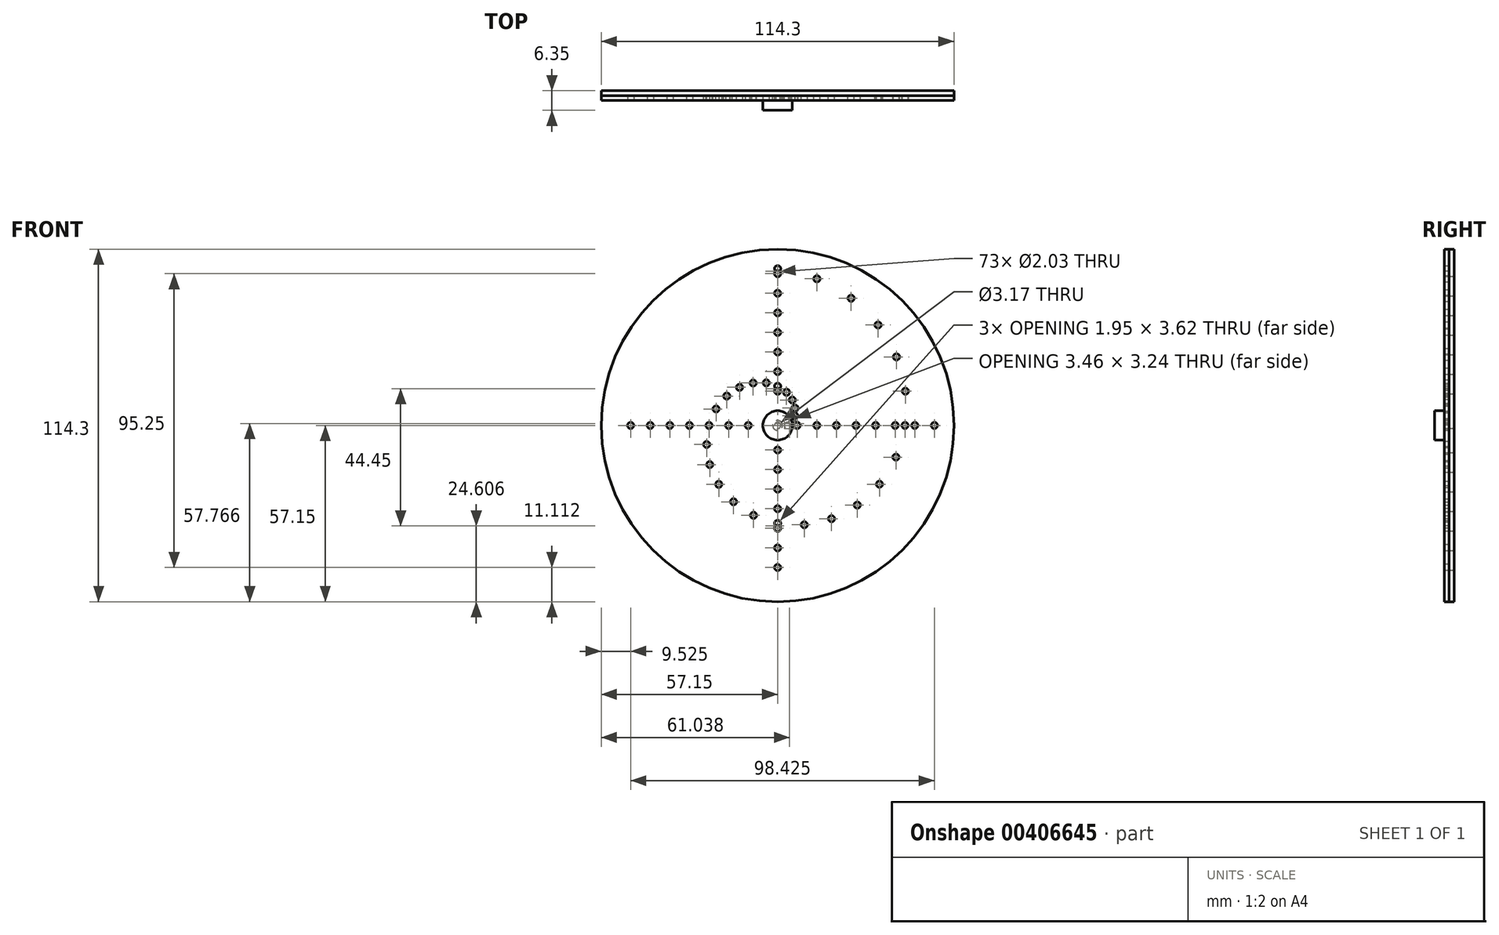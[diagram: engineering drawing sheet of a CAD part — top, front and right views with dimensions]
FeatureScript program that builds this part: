
annotation { "Feature Type Name" : "Feature", "Feature Type Description" : "" }
export const myFeature = defineFeature(function(context is Context, id is Id, definition is map)
    precondition{}
    {
        {
            var Q0;
            Q0=qCreatedBy(makeId("Front.planeOp"),FACE);
            var sketch = newSketch(context, id + "F0", { "sketchPlane" : qUnion([Q0])});
            skCircle(sketch, "E0", {"center": v(0, 0) * mm, "radius": 50.8 * mm, "construction": true});
            skCircle(sketch, "E1", {"center": v(0, 0) * mm, "radius": 1.59 * mm});
            skCircle(sketch, "E2.0", {"center": v(0, 0) * mm, "radius": 3.17 * mm, "construction": true});
            skCircle(sketch, "E3.0", {"center": v(0, 0) * mm, "radius": 4.76 * mm, "construction": true});
            skCircle(sketch, "E4.0", {"center": v(0, 0) * mm, "radius": 6.35 * mm, "construction": true});
            skLineSegment(sketch, "E5", {"start": v(0, 0) * mm, "end": v(67.63, 0) * mm, "construction": true});
            skCircle(sketch, "E6", {"center": v(3.17, 0) * mm, "radius": 1.02 * mm});
            skLineSegment(sketch, "E7", {"start": v(0, 0) * mm, "end": v(1.59, 0) * mm});
            skLineSegment(sketch, "E8", {"start": v(0, 0) * mm, "end": v(49.07, 13.15) * mm, "construction": true});
            skLineSegment(sketch, "E9.1.0", {"start": v(0, 0) * mm, "end": v(44, 25.4) * mm, "construction": true});
            skLineSegment(sketch, "E9.2.0", {"start": v(0, 0) * mm, "end": v(35.92, 35.92) * mm, "construction": true});
            skLineSegment(sketch, "E9.3.0", {"start": v(0, 0) * mm, "end": v(25.4, 44) * mm, "construction": true});
            skLineSegment(sketch, "E9.4.0", {"start": v(0, 0) * mm, "end": v(13.15, 49.07) * mm, "construction": true});
            skLineSegment(sketch, "E9.5.0", {"start": v(0, 0) * mm, "end": v(0, 50.8) * mm, "construction": true});
            skLineSegment(sketch, "E9.6.0", {"start": v(0, 0) * mm, "end": v(-13.15, 49.07) * mm, "construction": true});
            skLineSegment(sketch, "E9.7.0", {"start": v(0, 0) * mm, "end": v(-25.4, 44) * mm, "construction": true});
            skLineSegment(sketch, "E9.8.0", {"start": v(0, 0) * mm, "end": v(-35.92, 35.92) * mm, "construction": true});
            skLineSegment(sketch, "E9.9.0", {"start": v(0, 0) * mm, "end": v(-44, 25.4) * mm, "construction": true});
            skLineSegment(sketch, "E9.10.0", {"start": v(0, 0) * mm, "end": v(-49.07, 13.15) * mm, "construction": true});
            skLineSegment(sketch, "E9.11.0", {"start": v(0, 0) * mm, "end": v(-50.8, 0) * mm, "construction": true});
            skLineSegment(sketch, "E9.anchor2", {"start": v(0, 0) * mm, "end": v(-50.8, 0) * mm, "construction": true});
            skCircle(sketch, "E10.0", {"center": v(0, 0) * mm, "radius": 7.94 * mm, "construction": true});
            skCircle(sketch, "E11.0", {"center": v(0, 0) * mm, "radius": 9.53 * mm, "construction": true});
            skCircle(sketch, "E12.0", {"center": v(0, 0) * mm, "radius": 11.11 * mm, "construction": true});
            skCircle(sketch, "E13.0", {"center": v(0, 0) * mm, "radius": 12.7 * mm, "construction": true});
            skCircle(sketch, "E14.0", {"center": v(0, 0) * mm, "radius": 14.29 * mm, "construction": true});
            skCircle(sketch, "E15.0", {"center": v(0, 0) * mm, "radius": 15.88 * mm, "construction": true});
            skCircle(sketch, "E16.0", {"center": v(0, 0) * mm, "radius": 17.46 * mm, "construction": true});
            skCircle(sketch, "E17.0", {"center": v(0, 0) * mm, "radius": 19.05 * mm, "construction": true});
            skCircle(sketch, "E18.0", {"center": v(0, 0) * mm, "radius": 20.64 * mm, "construction": true});
            skCircle(sketch, "E19.0", {"center": v(0, 0) * mm, "radius": 22.22 * mm, "construction": true});
            skCircle(sketch, "E20.0", {"center": v(0, 0) * mm, "radius": 23.81 * mm, "construction": true});
            skCircle(sketch, "E21.0", {"center": v(0, 0) * mm, "radius": 25.4 * mm, "construction": true});
            skCircle(sketch, "E22.0", {"center": v(0, 0) * mm, "radius": 26.99 * mm, "construction": true});
            skCircle(sketch, "E23.0", {"center": v(0, 0) * mm, "radius": 28.57 * mm, "construction": true});
            skCircle(sketch, "E24.0", {"center": v(0, 0) * mm, "radius": 30.16 * mm, "construction": true});
            skCircle(sketch, "E25.0", {"center": v(0, 0) * mm, "radius": 31.75 * mm, "construction": true});
            skCircle(sketch, "E26", {"center": v(4.6, 1.23) * mm, "radius": 1.02 * mm});
            skCircle(sketch, "E27", {"center": v(5.5, 3.17) * mm, "radius": 1.02 * mm});
            skCircle(sketch, "E28", {"center": v(5.61, 5.61) * mm, "radius": 1.02 * mm});
            skCircle(sketch, "E29", {"center": v(4.76, 8.25) * mm, "radius": 1.02 * mm});
            skCircle(sketch, "E30", {"center": v(2.88, 10.73) * mm, "radius": 1.02 * mm});
            skCircle(sketch, "E31", {"center": v(0, 12.7) * mm, "radius": 1.02 * mm});
            skCircle(sketch, "E32", {"center": v(-3.7, 13.8) * mm, "radius": 1.02 * mm});
            skCircle(sketch, "E33", {"center": v(-7.94, 13.75) * mm, "radius": 1.02 * mm});
            skCircle(sketch, "E34", {"center": v(-12.35, 12.35) * mm, "radius": 1.02 * mm});
            skCircle(sketch, "E35", {"center": v(-16.5, 9.53) * mm, "radius": 1.02 * mm});
            skCircle(sketch, "E36", {"center": v(-19.93, 5.34) * mm, "radius": 1.02 * mm});
            skCircle(sketch, "E37", {"center": v(-22.22, 0) * mm, "radius": 1.02 * mm});
            skCircle(sketch, "E38.0", {"center": v(0, 0) * mm, "radius": 33.34 * mm, "construction": true});
            skCircle(sketch, "E39.0", {"center": v(0, 0) * mm, "radius": 34.92 * mm, "construction": true});
            skCircle(sketch, "E40.0", {"center": v(0, 0) * mm, "radius": 36.51 * mm, "construction": true});
            skCircle(sketch, "E41.0", {"center": v(0, 0) * mm, "radius": 38.1 * mm, "construction": true});
            skCircle(sketch, "E42.0", {"center": v(0, 0) * mm, "radius": 39.69 * mm, "construction": true});
            skCircle(sketch, "E43.0", {"center": v(0, 0) * mm, "radius": 41.27 * mm, "construction": true});
            skCircle(sketch, "E44.0", {"center": v(0, 0) * mm, "radius": 42.86 * mm, "construction": true});
            skCircle(sketch, "E45.0", {"center": v(0, 0) * mm, "radius": 44.45 * mm, "construction": true});
            skCircle(sketch, "E46.0", {"center": v(0, 0) * mm, "radius": 46.04 * mm, "construction": true});
            skCircle(sketch, "E47.0", {"center": v(0, 0) * mm, "radius": 47.62 * mm, "construction": true});
            skCircle(sketch, "E48.0", {"center": v(0, 0) * mm, "radius": 49.21 * mm, "construction": true});
            skLineSegment(sketch, "E49.MirrorCS", {"start": v(0, 0) * mm, "end": v(-49.07, -13.15) * mm, "construction": true});
            skLineSegment(sketch, "E50.MirrorCS", {"start": v(0, 0) * mm, "end": v(-44, -25.4) * mm, "construction": true});
            skLineSegment(sketch, "E51.MirrorCS", {"start": v(0, 0) * mm, "end": v(-35.92, -35.92) * mm, "construction": true});
            skLineSegment(sketch, "E52.MirrorCS", {"start": v(0, 0) * mm, "end": v(-25.4, -44) * mm, "construction": true});
            skLineSegment(sketch, "E53.MirrorCS", {"start": v(0, 0) * mm, "end": v(-13.15, -49.07) * mm, "construction": true});
            skLineSegment(sketch, "E54.MirrorCS", {"start": v(0, 0) * mm, "end": v(0, -50.8) * mm, "construction": true});
            skLineSegment(sketch, "E55.MirrorCS", {"start": v(0, 0) * mm, "end": v(13.15, -49.07) * mm, "construction": true});
            skLineSegment(sketch, "E56.MirrorCS", {"start": v(0, 0) * mm, "end": v(25.4, -44) * mm, "construction": true});
            skLineSegment(sketch, "E57.MirrorCS", {"start": v(0, 0) * mm, "end": v(35.92, -35.92) * mm, "construction": true});
            skLineSegment(sketch, "E58.MirrorCS", {"start": v(0, 0) * mm, "end": v(44, -25.4) * mm, "construction": true});
            skLineSegment(sketch, "E59.MirrorCS", {"start": v(0, 0) * mm, "end": v(49.07, -13.15) * mm, "construction": true});
            skCircle(sketch, "E60", {"center": v(-23, -6.16) * mm, "radius": 1.02 * mm});
            skCircle(sketch, "E61", {"center": v(-22, -12.7) * mm, "radius": 1.02 * mm});
            skCircle(sketch, "E62", {"center": v(-19.08, -19.08) * mm, "radius": 1.02 * mm});
            skCircle(sketch, "E63", {"center": v(-14.29, -24.75) * mm, "radius": 1.02 * mm});
            skCircle(sketch, "E64", {"center": v(-7.8, -29.13) * mm, "radius": 1.02 * mm});
            skCircle(sketch, "E65", {"center": v(0, -31.75) * mm, "radius": 1.02 * mm});
            skCircle(sketch, "E66", {"center": v(8.63, -32.2) * mm, "radius": 1.02 * mm});
            skCircle(sketch, "E67", {"center": v(17.46, -30.25) * mm, "radius": 1.02 * mm});
            skCircle(sketch, "E68", {"center": v(25.82, -25.82) * mm, "radius": 1.02 * mm});
            skCircle(sketch, "E69", {"center": v(33, -19.05) * mm, "radius": 1.02 * mm});
            skCircle(sketch, "E70", {"center": v(38.34, -10.27) * mm, "radius": 1.02 * mm});
            skCircle(sketch, "E71", {"center": v(41.27, 0) * mm, "radius": 1.02 * mm});
            skCircle(sketch, "E72", {"center": v(41.4, 11.1) * mm, "radius": 1.02 * mm});
            skCircle(sketch, "E73", {"center": v(38.5, 22.22) * mm, "radius": 1.02 * mm});
            skCircle(sketch, "E74", {"center": v(32.55, 32.55) * mm, "radius": 1.02 * mm});
            skCircle(sketch, "E75", {"center": v(23.81, 41.24) * mm, "radius": 1.02 * mm});
            skCircle(sketch, "E76", {"center": v(12.74, 47.54) * mm, "radius": 1.02 * mm});
            skCircle(sketch, "E77.0", {"center": v(0, 0) * mm, "radius": 57.15 * mm});
            skCircle(sketch, "E78", {"center": v(0, 50.8) * mm, "radius": 1.02 * mm});
            skSolve(sketch);
        }
        {
            var Q0;
            Q0 = qSketchRegion(id + "F0", true);
            extrude(context, id + "F1", {"entities" : qUnion([Q0]), "depth" : 1.59 * mm});
        }
        {
            var Q0;
            Q0=makeQuery(id+"F1.opExtrude","CAP_FACE",FACE,{"disambiguationData":[OSD([sQuery(id+"F0.wireOp",EDGE,"E1"),sQuery(id+"F0.wireOp",EDGE,"E6"),sQuery(id+"F0.wireOp",EDGE,"E26"),sQuery(id+"F0.wireOp",EDGE,"E27"),sQuery(id+"F0.wireOp",EDGE,"E28"),sQuery(id+"F0.wireOp",EDGE,"E29"),sQuery(id+"F0.wireOp",EDGE,"E30"),sQuery(id+"F0.wireOp",EDGE,"E31"),sQuery(id+"F0.wireOp",EDGE,"E32"),sQuery(id+"F0.wireOp",EDGE,"E33"),sQuery(id+"F0.wireOp",EDGE,"E34"),sQuery(id+"F0.wireOp",EDGE,"E35"),sQuery(id+"F0.wireOp",EDGE,"E36"),sQuery(id+"F0.wireOp",EDGE,"E37"),sQuery(id+"F0.wireOp",EDGE,"E60"),sQuery(id+"F0.wireOp",EDGE,"E61"),sQuery(id+"F0.wireOp",EDGE,"E62"),sQuery(id+"F0.wireOp",EDGE,"E63"),sQuery(id+"F0.wireOp",EDGE,"E64"),sQuery(id+"F0.wireOp",EDGE,"E65"),sQuery(id+"F0.wireOp",EDGE,"E66"),sQuery(id+"F0.wireOp",EDGE,"E67"),sQuery(id+"F0.wireOp",EDGE,"E68"),sQuery(id+"F0.wireOp",EDGE,"E69"),sQuery(id+"F0.wireOp",EDGE,"E70"),sQuery(id+"F0.wireOp",EDGE,"E71"),sQuery(id+"F0.wireOp",EDGE,"E72"),sQuery(id+"F0.wireOp",EDGE,"E73"),sQuery(id+"F0.wireOp",EDGE,"E74"),sQuery(id+"F0.wireOp",EDGE,"E75"),sQuery(id+"F0.wireOp",EDGE,"E76"),sQuery(id+"F0.wireOp",EDGE,"E77.0"),sQuery(id+"F0.wireOp",EDGE,"E78")])],"isStart":false});
            var sketch = newSketch(context, id + "F2", { "sketchPlane" : qUnion([Q0])});
            skCircle(sketch, "E79.0", {"center": v(0, 0) * mm, "radius": 57.15 * mm, "construction": true});
            skCircle(sketch, "E80", {"center": v(0, 0) * mm, "radius": 12.7 * mm});
            skCircle(sketch, "E81", {"center": v(0, 0) * mm, "radius": 25.4 * mm});
            skCircle(sketch, "E82", {"center": v(0, 0) * mm, "radius": 38.1 * mm});
            skCircle(sketch, "E83", {"center": v(0, 0) * mm, "radius": 6.35 * mm});
            skCircle(sketch, "E84", {"center": v(0, 0) * mm, "radius": 19.05 * mm});
            skCircle(sketch, "E85", {"center": v(0, 0) * mm, "radius": 31.75 * mm});
            skCircle(sketch, "E86", {"center": v(0, 0) * mm, "radius": 44.45 * mm});
            skCircle(sketch, "E87", {"center": v(0, 0) * mm, "radius": 50.8 * mm});
            skSolve(sketch);
        }
        {
            var Q0;
            Q0=makeQuery(id+"F2.imprint","IMPRINT",FACE,{"disambiguationData":[TD([[makeQuery(id+"F2.imprint","IMPRINT",EDGE,{"derivedFrom":makeQuery(id+"F1.opExtrude","CAP_EDGE",EDGE,{"disambiguationData":[OSD([sQuery(id+"F0.wireOp",EDGE,"E74")])],"isStart":false})}),-1.0]])]});
            var sketch = newSketch(context, id + "F3", { "sketchPlane" : qUnion([Q0])});
            skCircle(sketch, "E88", {"center": v(0, 0) * mm, "radius": 4.76 * mm});
            skSolve(sketch);
        }
        {
            var Q0;
            Q0 = qSketchRegion(id + "F3", true);
            extrude(context, id + "F4", {"entities" : qUnion([Q0]), "depth" : 3.17 * mm});
        }
        {
            var Q0;
            Q0=makeQuery(id+"F2.imprint","IMPRINT",FACE,{"disambiguationData":[TD([[makeQuery(id+"F2.imprint","IMPRINT",EDGE,{"derivedFrom":makeQuery(id+"F1.opExtrude","CAP_EDGE",EDGE,{"disambiguationData":[OSD([sQuery(id+"F0.wireOp",EDGE,"E77.0")])],"isStart":false})}),1.0]])]});
            var sketch = newSketch(context, id + "F5", { "sketchPlane" : qUnion([Q0])});
            skCircle(sketch, "E89.0", {"center": v(0, 0) * mm, "radius": 57.15 * mm});
            skCircle(sketch, "E89.1", {"center": v(0, 0) * mm, "radius": 50.8 * mm, "construction": true});
            skCircle(sketch, "E89.2", {"center": v(0, 0) * mm, "radius": 44.45 * mm, "construction": true});
            skCircle(sketch, "E89.3", {"center": v(0, 0) * mm, "radius": 38.1 * mm, "construction": true});
            skCircle(sketch, "E89.4", {"center": v(0, 0) * mm, "radius": 31.75 * mm, "construction": true});
            skCircle(sketch, "E89.5", {"center": v(0, 0) * mm, "radius": 25.4 * mm, "construction": true});
            skCircle(sketch, "E89.6", {"center": v(0, 0) * mm, "radius": 19.05 * mm, "construction": true});
            skCircle(sketch, "E89.7", {"center": v(0, 0) * mm, "radius": 12.7 * mm, "construction": true});
            skCircle(sketch, "E89.8", {"center": v(0, 0) * mm, "radius": 6.35 * mm, "construction": true});
            skLineSegment(sketch, "E90", {"start": v(0, 0) * mm, "end": v(57.15, 0) * mm, "construction": true});
            skCircle(sketch, "E91", {"center": v(6.35, 0) * mm, "radius": 1.02 * mm});
            skCircle(sketch, "E92", {"center": v(12.7, 0) * mm, "radius": 1.02 * mm});
            skCircle(sketch, "E93", {"center": v(19.05, 0) * mm, "radius": 1.02 * mm});
            skCircle(sketch, "E94", {"center": v(25.4, 0) * mm, "radius": 1.02 * mm});
            skCircle(sketch, "E95", {"center": v(31.75, 0) * mm, "radius": 1.02 * mm});
            skCircle(sketch, "E96", {"center": v(38.1, 0) * mm, "radius": 1.02 * mm});
            skCircle(sketch, "E97", {"center": v(44.45, 0) * mm, "radius": 1.02 * mm});
            skCircle(sketch, "E98", {"center": v(50.8, 0) * mm, "radius": 1.02 * mm});
            skCircle(sketch, "E99.0", {"center": v(5.61, 5.61) * mm, "radius": 1.02 * mm, "construction": true});
            skLineSegment(sketch, "E100.anchor1", {"start": v(0, 0) * mm, "end": v(6.35, 0) * mm, "construction": true});
            skCircle(sketch, "E101", {"center": v(0, 0) * mm, "radius": 57.15 * mm, "construction": true});
            skCircle(sketch, "E102.1.0", {"center": v(0, -25.4) * mm, "radius": 1.02 * mm, "construction": true});
            skCircle(sketch, "E102.1.1", {"center": v(0, -19.05) * mm, "radius": 1.02 * mm, "construction": true});
            skCircle(sketch, "E102.1.2", {"center": v(0, -12.7) * mm, "radius": 1.02 * mm, "construction": true});
            skCircle(sketch, "E102.1.3", {"center": v(0, -38.1) * mm, "radius": 1.02 * mm, "construction": true});
            skCircle(sketch, "E102.1.4", {"center": v(0, -31.75) * mm, "radius": 1.02 * mm, "construction": true});
            skCircle(sketch, "E102.1.5", {"center": v(0, -44.45) * mm, "radius": 1.02 * mm, "construction": true});
            skCircle(sketch, "E102.1.6", {"center": v(0, -50.8) * mm, "radius": 1.02 * mm, "construction": true});
            skCircle(sketch, "E102.1.7", {"center": v(0, -6.35) * mm, "radius": 1.02 * mm, "construction": true});
            skCircle(sketch, "E102.2.0", {"center": v(-25.4, 0) * mm, "radius": 1.02 * mm, "construction": true});
            skCircle(sketch, "E102.2.1", {"center": v(-19.05, 0) * mm, "radius": 1.02 * mm, "construction": true});
            skCircle(sketch, "E102.2.2", {"center": v(-12.7, 0) * mm, "radius": 1.02 * mm, "construction": true});
            skCircle(sketch, "E102.2.3", {"center": v(-38.1, 0) * mm, "radius": 1.02 * mm, "construction": true});
            skCircle(sketch, "E102.2.4", {"center": v(-31.75, 0) * mm, "radius": 1.02 * mm, "construction": true});
            skCircle(sketch, "E102.2.5", {"center": v(-44.45, 0) * mm, "radius": 1.02 * mm, "construction": true});
            skCircle(sketch, "E102.2.6", {"center": v(-50.8, 0) * mm, "radius": 1.02 * mm, "construction": true});
            skCircle(sketch, "E102.2.7", {"center": v(-6.35, 0) * mm, "radius": 1.02 * mm, "construction": true});
            skCircle(sketch, "E102.3.0", {"center": v(0, 25.4) * mm, "radius": 1.02 * mm, "construction": true});
            skCircle(sketch, "E102.3.1", {"center": v(0, 19.05) * mm, "radius": 1.02 * mm, "construction": true});
            skCircle(sketch, "E102.3.2", {"center": v(0, 12.7) * mm, "radius": 1.02 * mm, "construction": true});
            skCircle(sketch, "E102.3.3", {"center": v(0, 38.1) * mm, "radius": 1.02 * mm, "construction": true});
            skCircle(sketch, "E102.3.4", {"center": v(0, 31.75) * mm, "radius": 1.02 * mm, "construction": true});
            skCircle(sketch, "E102.3.5", {"center": v(0, 44.45) * mm, "radius": 1.02 * mm, "construction": true});
            skCircle(sketch, "E102.3.6", {"center": v(0, 50.8) * mm, "radius": 1.02 * mm, "construction": true});
            skCircle(sketch, "E102.3.7", {"center": v(0, 6.35) * mm, "radius": 1.02 * mm, "construction": true});
            skLineSegment(sketch, "E102.anchor2", {"start": v(0, 0) * mm, "end": v(0, 6.35) * mm, "construction": true});
            skSolve(sketch);
        }
        {
            var Q0;
            Q0 = qSketchRegion(id + "F5", true);
            extrude(context, id + "F6", {"entities" : qUnion([Q0]), "oppositeDirection" : true, "depth" : 3.17 * mm});
        }
        {
            var Q0;
            Q0=makeQuery(id+"F2.imprint","IMPRINT",FACE,{"disambiguationData":[TD([[makeQuery(id+"F2.imprint","IMPRINT",EDGE,{"derivedFrom":makeQuery(id+"F1.opExtrude","CAP_EDGE",EDGE,{"disambiguationData":[OSD([sQuery(id+"F0.wireOp",EDGE,"E77.0")])],"isStart":false})}),1.0]])]});
            var sketch = newSketch(context, id + "F7", { "sketchPlane" : qUnion([Q0])});
            skCircle(sketch, "E103.0", {"center": v(0, -6.35) * mm, "radius": 1.02 * mm, "construction": true});
            skLineSegment(sketch, "E104", {"start": v(0, 0) * mm, "end": v(0, -57.15) * mm, "construction": true});
            skCircle(sketch, "E105.0", {"center": v(0, 0) * mm, "radius": 57.15 * mm, "construction": true});
            skCircle(sketch, "E106.2", {"center": v(0, -12.7) * mm, "radius": 1.02 * mm, "construction": true});
            skCircle(sketch, "E106.3", {"center": v(0, -19.05) * mm, "radius": 1.02 * mm, "construction": true});
            skCircle(sketch, "E106.4", {"center": v(0, -25.4) * mm, "radius": 1.02 * mm, "construction": true});
            skCircle(sketch, "E106.5", {"center": v(0, -31.75) * mm, "radius": 1.02 * mm, "construction": true});
            skCircle(sketch, "E106.6", {"center": v(0, -38.1) * mm, "radius": 1.02 * mm, "construction": true});
            skCircle(sketch, "E106.7", {"center": v(0, -44.45) * mm, "radius": 1.02 * mm, "construction": true});
            skCircle(sketch, "E106.8", {"center": v(0, -50.8) * mm, "radius": 1.02 * mm, "construction": true});
            skCircle(sketch, "E107.0.1.0", {"center": v(0, -33.34) * mm, "radius": 1.02 * mm});
            skCircle(sketch, "E107.0.1.1", {"center": v(0, -52.39) * mm, "radius": 1.02 * mm, "construction": true});
            skCircle(sketch, "E107.0.1.2", {"center": v(0, -26.99) * mm, "radius": 1.02 * mm});
            skCircle(sketch, "E107.0.1.3", {"center": v(0, -14.29) * mm, "radius": 1.02 * mm});
            skCircle(sketch, "E107.0.1.4", {"center": v(0, -20.64) * mm, "radius": 1.02 * mm});
            skCircle(sketch, "E107.0.1.5", {"center": v(0, -39.69) * mm, "radius": 1.02 * mm});
            skCircle(sketch, "E107.0.1.6", {"center": v(0, -46.04) * mm, "radius": 1.02 * mm});
            skCircle(sketch, "E107.0.1.7", {"center": v(0, -7.94) * mm, "radius": 1.02 * mm});
            skLineSegment(sketch, "E107.direction1", {"start": v(0, -50.8) * mm, "end": v(25.4, -50.8) * mm, "construction": true});
            skLineSegment(sketch, "E107.direction2", {"start": v(0, -50.8) * mm, "end": v(0, -52.39) * mm, "construction": true});
            skSolve(sketch);
        }
        {
            var Q0;
            Q0 = qSketchRegion(id + "F7", true);
            extrude(context, id + "F8", {"entities" : qUnion([Q0]), "operationType" : NewBodyOperationType.REMOVE, "endBound" : BoundingType.THROUGH_ALL, "oppositeDirection" : true, "depth" : 25.4 * mm});
        }
        {
            var Q0;
            Q0=makeQuery(id+"F2.imprint","IMPRINT",FACE,{"disambiguationData":[TD([[makeQuery(id+"F2.imprint","IMPRINT",EDGE,{"derivedFrom":makeQuery(id+"F1.opExtrude","CAP_EDGE",EDGE,{"disambiguationData":[OSD([sQuery(id+"F0.wireOp",EDGE,"E28")])],"isStart":false})}),-1.0]])]});
            var sketch = newSketch(context, id + "F9", { "sketchPlane" : qUnion([Q0])});
            skCircle(sketch, "E108.0", {"center": v(-6.35, 0) * mm, "radius": 1.02 * mm, "construction": true});
            skCircle(sketch, "E109", {"center": v(-9.53, 0) * mm, "radius": 1.02 * mm});
            skCircle(sketch, "E110.0", {"center": v(0, 6.35) * mm, "radius": 1.02 * mm, "construction": true});
            skCircle(sketch, "E111", {"center": v(0, 11.11) * mm, "radius": 1.02 * mm});
            skCircle(sketch, "E112.1.0.0", {"center": v(-15.88, 0) * mm, "radius": 1.02 * mm});
            skCircle(sketch, "E112.2.0.0", {"center": v(-22.23, 0) * mm, "radius": 1.02 * mm});
            skCircle(sketch, "E112.3.0.0", {"center": v(-28.58, 0) * mm, "radius": 1.02 * mm});
            skCircle(sketch, "E112.4.0.0", {"center": v(-34.93, 0) * mm, "radius": 1.02 * mm});
            skCircle(sketch, "E112.5.0.0", {"center": v(-41.28, 0) * mm, "radius": 1.02 * mm});
            skCircle(sketch, "E112.6.0.0", {"center": v(-47.62, 0) * mm, "radius": 1.02 * mm});
            skLineSegment(sketch, "E112.direction1", {"start": v(-9.53, 0) * mm, "end": v(-15.88, 0) * mm, "construction": true});
            skCircle(sketch, "E113.0.1.0", {"center": v(0, 17.46) * mm, "radius": 1.02 * mm});
            skCircle(sketch, "E113.0.2.0", {"center": v(0, 23.81) * mm, "radius": 1.02 * mm});
            skCircle(sketch, "E113.0.3.0", {"center": v(0, 30.16) * mm, "radius": 1.02 * mm});
            skCircle(sketch, "E113.0.4.0", {"center": v(0, 36.51) * mm, "radius": 1.02 * mm});
            skCircle(sketch, "E113.0.5.0", {"center": v(0, 42.86) * mm, "radius": 1.02 * mm});
            skCircle(sketch, "E113.0.6.0", {"center": v(0, 49.21) * mm, "radius": 1.02 * mm});
            skLineSegment(sketch, "E113.direction1", {"start": v(0, 11.11) * mm, "end": v(14.01, 11.11) * mm, "construction": true});
            skLineSegment(sketch, "E113.direction2", {"start": v(0, 11.11) * mm, "end": v(0, 17.46) * mm, "construction": true});
            skSolve(sketch);
        }
        {
            var Q0;
            Q0 = qSketchRegion(id + "F9", true);
            var Q1;
            Q1=makeQuery(id+"F6.opExtrude","CAP_FACE",FACE,{"disambiguationData":[OSD([sQuery(id+"F5.wireOp",EDGE,"E89.0"),sQuery(id+"F5.wireOp",EDGE,"E91"),sQuery(id+"F5.wireOp",EDGE,"E92"),sQuery(id+"F5.wireOp",EDGE,"E93"),sQuery(id+"F5.wireOp",EDGE,"E94"),sQuery(id+"F5.wireOp",EDGE,"E95"),sQuery(id+"F5.wireOp",EDGE,"E96"),sQuery(id+"F5.wireOp",EDGE,"E97"),sQuery(id+"F5.wireOp",EDGE,"E98")])],"isStart":false});
            extrude(context, id + "F10", {"entities" : qUnion([Q0]), "operationType" : NewBodyOperationType.REMOVE, "endBound" : BoundingType.UP_TO_SURFACE, "oppositeDirection" : true, "endBoundEntityFace" : qUnion([Q1]), "depth" : 25.4 * mm});
        }
        {
            var Q0;
            Q0=makeQuery(id+"F2.imprint","IMPRINT",FACE,{"disambiguationData":[TD([[makeQuery(id+"F2.imprint","IMPRINT",EDGE,{"derivedFrom":makeQuery(id+"F1.opExtrude","CAP_EDGE",EDGE,{"disambiguationData":[OSD([sQuery(id+"F0.wireOp",EDGE,"E1")])],"isStart":false})}),-1.0]])]});
            var sketch = newSketch(context, id + "F11", { "sketchPlane" : qUnion([Q0])});
            skPoint(sketch, "E114.0", {"position": v(0, 0) * mm});
            skCircle(sketch, "E115", {"center": v(0, 0) * mm, "radius": 1.02 * mm});
            skCircle(sketch, "E116.0", {"center": v(-9.53, 0) * mm, "radius": 1.02 * mm, "construction": true});
            skSolve(sketch);
        }
        {
            var Q0;
            Q0 = qSketchRegion(id + "F11", true);
            extrude(context, id + "F12", {"entities" : qUnion([Q0]), "operationType" : NewBodyOperationType.REMOVE, "endBound" : BoundingType.THROUGH_ALL, "oppositeDirection" : true, "depth" : 25.4 * mm});
        }
    });
